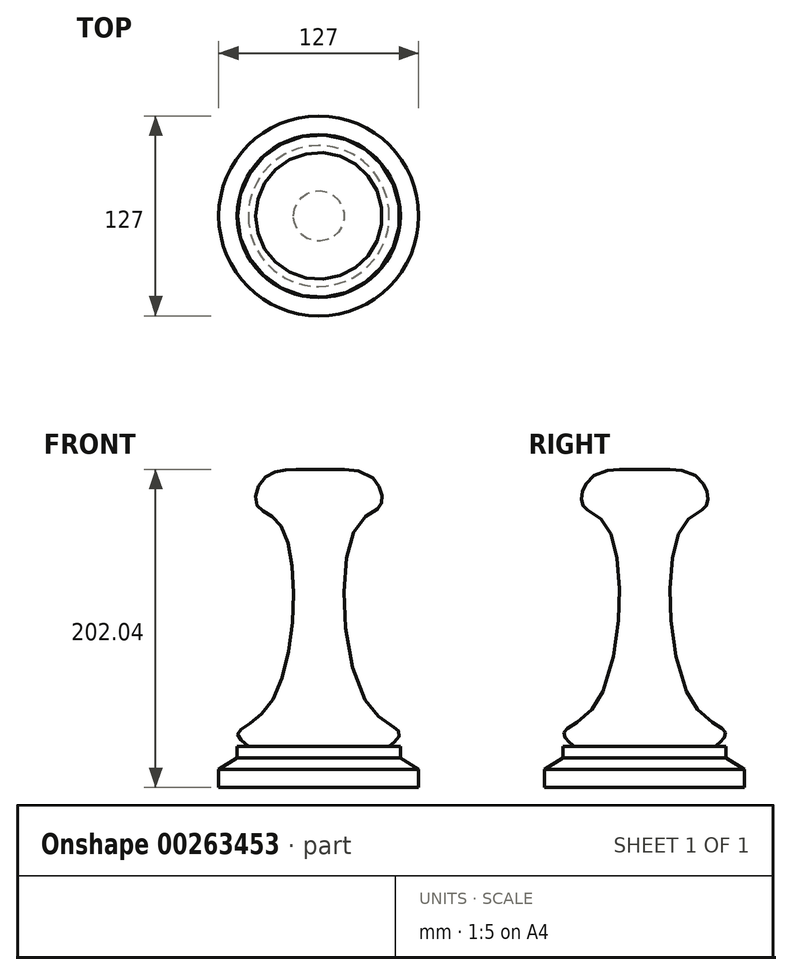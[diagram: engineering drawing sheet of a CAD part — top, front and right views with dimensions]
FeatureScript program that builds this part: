
annotation { "Feature Type Name" : "Feature", "Feature Type Description" : "" }
export const myFeature = defineFeature(function(context is Context, id is Id, definition is map)
    precondition{}
    {
        {
            var Q0;
            Q0=qCreatedBy(makeId("Front.planeOp"),FACE);
            var sketch = newSketch(context, id + "F0", { "sketchPlane" : qUnion([Q0])});
            skLineSegment(sketch, "E0", {"start": v(0, -126.22) * mm, "end": v(-63.5, -126.22) * mm});
            skLineSegment(sketch, "E1", {"start": v(-63.5, -126.22) * mm, "end": v(-63.5, -114.75) * mm});
            skLineSegment(sketch, "E2", {"start": v(-63.5, -114.75) * mm, "end": v(-51.78, -107.4) * mm});
            skLineSegment(sketch, "E3", {"start": v(-51.78, -107.4) * mm, "end": v(-51.78, -100.05) * mm});
            skLineSegment(sketch, "E4", {"start": v(-51.78, -100.05) * mm, "end": v(-44.75, -100.05) * mm});
            skFitSpline(sketch, "E5", {"points": [v(-44.75, -100.05) * mm, v(-51.46, -91.74) * mm, v(-30.36, -72.24) * mm, v(-23.65, 39.3) * mm, v(-39.31, 53.04) * mm, v(-34.52, 70.3) * mm, v(-15.02, 75.74) * mm, v(0, 75.74) * mm], "startDerivative": vector(-120.58, 98.24) * mm, "endDerivative": vector(131.93, -2.09) * mm});
            skLineSegment(sketch, "E6", {"start": v(0, 75.74) * mm, "end": v(0, -126.22) * mm});
            skSolve(sketch);
        }
        {
            var Q0;
            Q0 = qSketchRegion(id + "F0", true);
            var Q1;
            Q1=sQuery(id+"F0.wireOp",EDGE,"E6");
            revolve(context, id + "F1", {"entities" : qUnion([Q0]), "axis" : qUnion([Q1]), "revolveType" : RevolveType.FULL});
        }
    });
